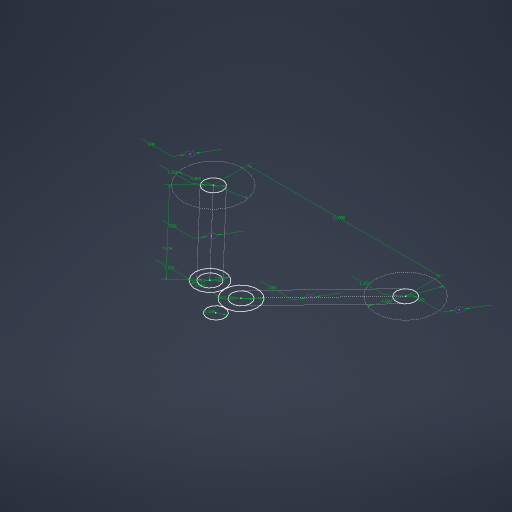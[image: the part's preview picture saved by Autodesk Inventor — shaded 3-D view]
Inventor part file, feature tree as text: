
AUTODESK INVENTOR PART (.ipt)
format: ipt  version: 2024.3 (Build 283343000, 343)  size: 182,784 bytes
history: native  units: in
note: dims shown in document units (in); Inventor stores cm internally (conversion verified against a paired STEP export)
features: sketch x1
ambient origin geometry x8: Origin, YZ Plane, XZ Plane, XY Plane, X Axis, Y Axis, Z Axis, Center Point
feature tree (1):
  sketch  "Sketch1"  dims[d0=1.2in d1=2.2in d2=2.0in d3=1.253in d4=1.253in d5=7.874in d6=13.0in d7=4.0in d8=4.0in d9=1.253in d10=1.253in d11=0.5in d12=0.5in d13=0.5in d14=0.5in]
